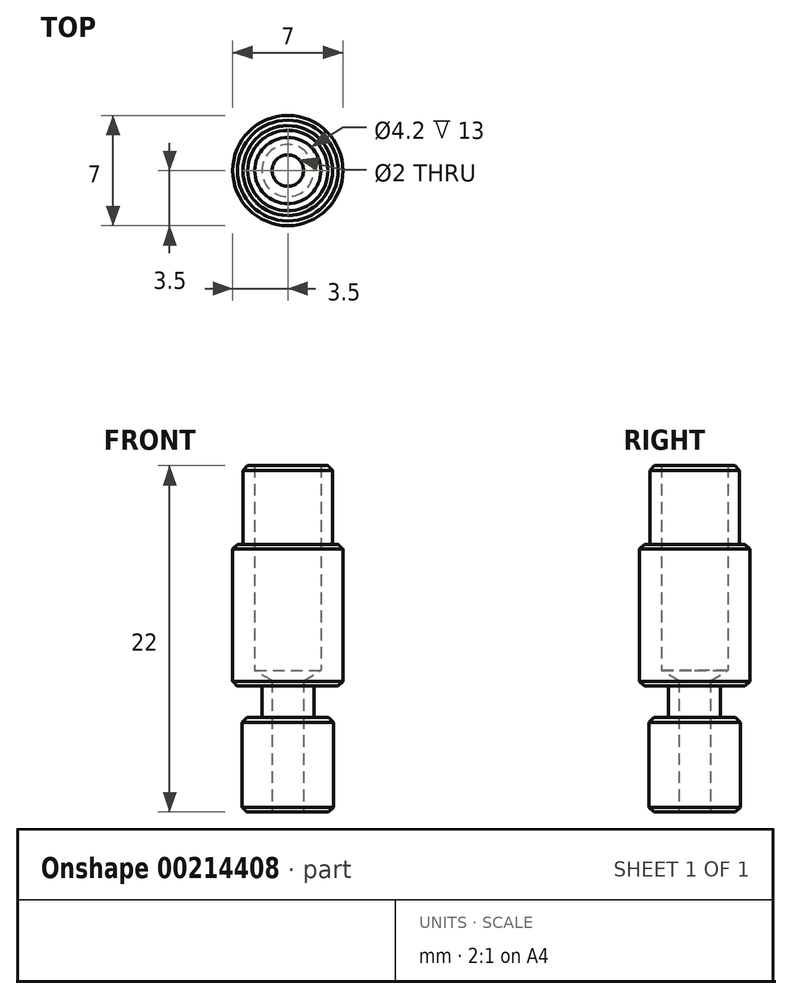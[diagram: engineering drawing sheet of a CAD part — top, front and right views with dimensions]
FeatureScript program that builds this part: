
annotation { "Feature Type Name" : "Feature", "Feature Type Description" : "" }
export const myFeature = defineFeature(function(context is Context, id is Id, definition is map)
    precondition{}
    {
        {
            var Q0;
            Q0=qCreatedBy(makeId("Front.planeOp"),FACE);
            var sketch = newSketch(context, id + "F0", { "sketchPlane" : qUnion([Q0])});
            skLineSegment(sketch, "E0", {"start": v(0, 0) * mm, "end": v(0, 22) * mm, "construction": true});
            skLineSegment(sketch, "E1", {"start": v(2.1, 22) * mm, "end": v(2.1, 9) * mm});
            skLineSegment(sketch, "E2", {"start": v(2.1, 9) * mm, "end": v(1, 8.34) * mm});
            skLineSegment(sketch, "E3", {"start": v(1, 8.34) * mm, "end": v(1, 0) * mm});
            skLineSegment(sketch, "E4", {"start": v(1, 0) * mm, "end": v(2.9, 0) * mm});
            skLineSegment(sketch, "E5", {"start": v(2.9, 0) * mm, "end": v(2.9, 6) * mm});
            skLineSegment(sketch, "E6", {"start": v(2.9, 6) * mm, "end": v(1.65, 6) * mm});
            skLineSegment(sketch, "E7", {"start": v(1.65, 6) * mm, "end": v(1.65, 8) * mm});
            skLineSegment(sketch, "E8", {"start": v(1.65, 8) * mm, "end": v(3.5, 8) * mm});
            skLineSegment(sketch, "E9", {"start": v(3.5, 8) * mm, "end": v(3.5, 17) * mm});
            skLineSegment(sketch, "E10", {"start": v(3.5, 17) * mm, "end": v(2.85, 17) * mm});
            skLineSegment(sketch, "E11", {"start": v(2.85, 17) * mm, "end": v(2.85, 22) * mm});
            skLineSegment(sketch, "E12", {"start": v(2.85, 22) * mm, "end": v(2.1, 22) * mm});
            skSolve(sketch);
        }
        {
            var Q0;
            Q0 = qSketchRegion(id + "F0", true);
            var Q1;
            Q1=sQuery(id+"F0.wireOp",EDGE,"E0");
            revolve(context, id + "F1", {"entities" : qUnion([Q0]), "axis" : qUnion([Q1]), "revolveType" : RevolveType.FULL});
        }
        {
            var Q0;
            Q0=makeQuery(id+"F1.opRevolve","SWEPT_EDGE",EDGE,{"disambiguationData":[OSD([sQuery(id+"F0.wireOp",EDGE,"E11"),sQuery(id+"F0.wireOp",EDGE,"E12")])]});
            var Q1;
            Q1=makeQuery(id+"F1.opRevolve","SWEPT_EDGE",EDGE,{"disambiguationData":[OSD([sQuery(id+"F0.wireOp",EDGE,"E9"),sQuery(id+"F0.wireOp",EDGE,"E10")])]});
            var Q2;
            Q2=makeQuery(id+"F1.opRevolve","SWEPT_EDGE",EDGE,{"disambiguationData":[OSD([sQuery(id+"F0.wireOp",EDGE,"E8"),sQuery(id+"F0.wireOp",EDGE,"E9")])]});
            var Q3;
            Q3=makeQuery(id+"F1.opRevolve","SWEPT_EDGE",EDGE,{"disambiguationData":[OSD([sQuery(id+"F0.wireOp",EDGE,"E5"),sQuery(id+"F0.wireOp",EDGE,"E6")])]});
            var Q4;
            Q4=makeQuery(id+"F1.opRevolve","SWEPT_EDGE",EDGE,{"disambiguationData":[OSD([sQuery(id+"F0.wireOp",EDGE,"E4"),sQuery(id+"F0.wireOp",EDGE,"E5")])]});
            chamfer(context, id + "F2", {"entities" : qUnion([Q0, Q1, Q2, Q3, Q4]), "width" : 0.3 * mm, "tangentPropagation" : true});
        }
    });
